# Revit family: RN 55044 Optipress-Therm-Vis de rappel
name_source: partatom
category: Rohrformteile
units: mm (PartAtom-declared; Revit-internal decimal feet)

## family parameters
Arbeitsebenenbasiert = Nein
Beim Laden mit Abzugskörper schneiden = Nein
Bemaßung runder Anschluss = Durchmesser verwenden
Gemeinsam genutzt = Nein
Immer vertikal = Ja
Teiletyp = Verbindung

## types (8) — shared parameters
1.010.00.2 Blattnummer der Richtlinie = 29
1.010.00.3 Ausgabedatum (Monat) der Richtlinie = 201308
1.010.00.4 Herstellername = R. Nussbaum AG
1.010.00.5 Revisionsdatum der Datei = 20190521
1.010.00.6 Webadresse des Herstellers = http://www.nussbaum.ch
1.100.00.4 Produktbezeichnung = Versorgung
1.110.00.2 Index = 1
1.110.00.4 Produktbezeichnung = Optipress-Therm
1.960/3L.00.8 Link (URL) = https://www.nussbaum.ch
29.700.00.4 Produktname = Optipress-Therm-Verschraubung, mit Innengewinde
29.700.00.5 Produktkennung = 2
29.700.00.6 Querschnittsform = 1
29.700.00.7 Nennweitensystem = DN
29.700.00.8 Nenndrucksystem = PN
29.710.02.4 Nenndruck = 16
29.710.02.5 max. zul. Überdruck [hPa] = 1600
29.710.02.7 max. zul. Dauer-Betriebsdruck [hPa] = 1600
29.710.02.9 max. zul. Dauer-Betriebstemperatur [°C] = 95
Connector Visibility = Nein
EnclosingSpace Visibility = Nein
Hersteller = R. Nussbaum AG

## per-type parameters (varying)
- DN=20x25: 1.800.00.3 TGA-Nummer=01900100000000000000000000000000000000000000000025000000000000000008; 1.800.00.4 Kommentarfeld=55044.30, Optipress-Therm-Verschraubung, mit Innengewinde, DN=20x25, L=77, Rp=1; 1.810.00.3 Hersteller-Bestellnummer=55044.3; 1.810.00.4 DATANORM-Nummer=55044.30; 1.810.00.5 StLB-Nummer=256.124; 1.810.00.6 GTIN-Nummer=7612945685797; 29.710.02.10 Formstück-Gewicht [kg]=0.252; 29.710.02.3 Benennung=Optipress-Therm-Verschraubung, mit Innengewinde, DN=20x25, L=77, Rp=1; CONNECTOR0_DIAMETER_dX_0r=20 mm; CONNECTOR0_dX_01=24 mm; CONNECTOR0_ref_dX=24 mm; CONNECTOR1_DIAMETER_dX_0r=25 mm  [stored 0.082021 ft]; CONNECTOR1_dX_00=60 mm; CONNECTOR1_dX_01=77 mm  [stored 0.252625 ft]; CONNECTOR1_ref_dX=60 mm; Modell=55044.3; R. Nussbaum AG 55044.22 de Visibility=Nein; R. Nussbaum AG 55044.23 de Visibility=Nein; R. Nussbaum AG 55044.25 de Visibility=Nein; R. Nussbaum AG 55044.26 de Visibility=Nein; R. Nussbaum AG 55044.27 de Visibility=Nein; R. Nussbaum AG 55044.28 de Visibility=Nein; R. Nussbaum AG 55044.29 de Visibility=Nein; R. Nussbaum AG 55044.30 de Visibility=Ja; Typenkommentare=Optipress-Therm-Vis de rappel DN=20x25
- DN=50: 1.800.00.3 TGA-Nummer=01900100000000000000000000000000000000000000000025000000000000000007; 1.800.00.4 Kommentarfeld=55044.29, Optipress-Therm-Verschraubung, mit Innengewinde, DN=50, L=87, Rp=2; 1.810.00.3 Hersteller-Bestellnummer=55044.29; 1.810.00.4 DATANORM-Nummer=55044.29; 1.810.00.5 StLB-Nummer=256.128; 1.810.00.6 GTIN-Nummer=7612945685834; 29.710.02.10 Formstück-Gewicht [kg]=0.801; 29.710.02.3 Benennung=Optipress-Therm-Verschraubung, mit Innengewinde, DN=50, L=87, Rp=2; CONNECTOR0_DIAMETER_dX_0r=50 mm; CONNECTOR0_dX_01=40 mm; CONNECTOR0_ref_dX=40 mm; CONNECTOR1_DIAMETER_dX_0r=50 mm; CONNECTOR1_dX_00=63 mm; CONNECTOR1_dX_01=87 mm; CONNECTOR1_ref_dX=63 mm; Modell=55044.29; R. Nussbaum AG 55044.22 de Visibility=Nein; R. Nussbaum AG 55044.23 de Visibility=Nein; R. Nussbaum AG 55044.25 de Visibility=Nein; R. Nussbaum AG 55044.26 de Visibility=Nein; R. Nussbaum AG 55044.27 de Visibility=Nein; R. Nussbaum AG 55044.28 de Visibility=Nein; R. Nussbaum AG 55044.29 de Visibility=Ja; R. Nussbaum AG 55044.30 de Visibility=Nein; Typenkommentare=Optipress-Therm-Vis de rappel DN=50
- DN=40: 1.800.00.3 TGA-Nummer=01900100000000000000000000000000000000000000000025000000000000000006; 1.800.00.4 Kommentarfeld=55044.28, Optipress-Therm-Verschraubung, mit Innengewinde, DN=40, L=91, Rp=1½; 1.810.00.3 Hersteller-Bestellnummer=55044.28; 1.810.00.4 DATANORM-Nummer=55044.28; 1.810.00.5 StLB-Nummer=256.127; 1.810.00.6 GTIN-Nummer=7612945685827; 29.710.02.10 Formstück-Gewicht [kg]=0.511; 29.710.02.3 Benennung=Optipress-Therm-Verschraubung, mit Innengewinde, DN=40, L=91, Rp=1½; CONNECTOR0_DIAMETER_dX_0r=40 mm; CONNECTOR0_dX_01=36 mm; CONNECTOR0_ref_dX=36 mm; CONNECTOR1_DIAMETER_dX_0r=40 mm; CONNECTOR1_dX_00=72 mm; CONNECTOR1_dX_01=91 mm; CONNECTOR1_ref_dX=72 mm; Modell=55044.28; R. Nussbaum AG 55044.22 de Visibility=Nein; R. Nussbaum AG 55044.23 de Visibility=Nein; R. Nussbaum AG 55044.25 de Visibility=Nein; R. Nussbaum AG 55044.26 de Visibility=Nein; R. Nussbaum AG 55044.27 de Visibility=Nein; R. Nussbaum AG 55044.28 de Visibility=Ja; R. Nussbaum AG 55044.29 de Visibility=Nein; R. Nussbaum AG 55044.30 de Visibility=Nein; Typenkommentare=Optipress-Therm-Vis de rappel DN=40
- DN=32: 1.800.00.3 TGA-Nummer=01900100000000000000000000000000000000000000000025000000000000000005; 1.800.00.4 Kommentarfeld=55044.27, Optipress-Therm-Verschraubung, mit Innengewinde, DN=32, L=78, Rp=1¼; 1.810.00.3 Hersteller-Bestellnummer=55044.27; 1.810.00.4 DATANORM-Nummer=55044.27; 1.810.00.5 StLB-Nummer=256.126; 1.810.00.6 GTIN-Nummer=7612945685810; 29.710.02.10 Formstück-Gewicht [kg]=0.359; 29.710.02.3 Benennung=Optipress-Therm-Verschraubung, mit Innengewinde, DN=32, L=78, Rp=1¼; CONNECTOR0_DIAMETER_dX_0r=32 mm; CONNECTOR0_dX_01=26 mm; CONNECTOR0_ref_dX=26 mm; CONNECTOR1_DIAMETER_dX_0r=32 mm; CONNECTOR1_dX_00=59 mm; CONNECTOR1_dX_01=78 mm; CONNECTOR1_ref_dX=59 mm; Modell=55044.27; R. Nussbaum AG 55044.22 de Visibility=Nein; R. Nussbaum AG 55044.23 de Visibility=Nein; R. Nussbaum AG 55044.25 de Visibility=Nein; R. Nussbaum AG 55044.26 de Visibility=Nein; R. Nussbaum AG 55044.27 de Visibility=Ja; R. Nussbaum AG 55044.28 de Visibility=Nein; R. Nussbaum AG 55044.29 de Visibility=Nein; R. Nussbaum AG 55044.30 de Visibility=Nein; Typenkommentare=Optipress-Therm-Vis de rappel DN=32
- DN=25: 1.800.00.3 TGA-Nummer=01900100000000000000000000000000000000000000000025000000000000000004; 1.800.00.4 Kommentarfeld=55044.26, Optipress-Therm-Verschraubung, mit Innengewinde, DN=25, L=88, Rp=1; 1.810.00.3 Hersteller-Bestellnummer=55044.26; 1.810.00.4 DATANORM-Nummer=55044.26; 1.810.00.5 StLB-Nummer=256.125; 1.810.00.6 GTIN-Nummer=7612945685803; 29.710.02.10 Formstück-Gewicht [kg]=0.278; 29.710.02.3 Benennung=Optipress-Therm-Verschraubung, mit Innengewinde, DN=25, L=88, Rp=1; CONNECTOR0_DIAMETER_dX_0r=25 mm  [stored 0.082021 ft]; CONNECTOR0_dX_01=24 mm; CONNECTOR0_ref_dX=24 mm; CONNECTOR1_DIAMETER_dX_0r=25 mm  [stored 0.082021 ft]; CONNECTOR1_dX_00=71 mm; CONNECTOR1_dX_01=88 mm; CONNECTOR1_ref_dX=71 mm; Modell=55044.26; R. Nussbaum AG 55044.22 de Visibility=Nein; R. Nussbaum AG 55044.23 de Visibility=Nein; R. Nussbaum AG 55044.25 de Visibility=Nein; R. Nussbaum AG 55044.26 de Visibility=Ja; R. Nussbaum AG 55044.27 de Visibility=Nein; R. Nussbaum AG 55044.28 de Visibility=Nein; R. Nussbaum AG 55044.29 de Visibility=Nein; R. Nussbaum AG 55044.30 de Visibility=Nein; Typenkommentare=Optipress-Therm-Vis de rappel DN=25
- DN=20: 1.800.00.3 TGA-Nummer=01900100000000000000000000000000000000000000000025000000000000000003; 1.800.00.4 Kommentarfeld=55044.25, Optipress-Therm-Verschraubung, mit Innengewinde, DN=20, L=76, Rp=¾; 1.810.00.3 Hersteller-Bestellnummer=55044.25; 1.810.00.4 DATANORM-Nummer=55044.25; 1.810.00.6 GTIN-Nummer=7612945685780; 29.710.02.10 Formstück-Gewicht [kg]=0.158; 29.710.02.3 Benennung=Optipress-Therm-Verschraubung, mit Innengewinde, DN=20, L=76, Rp=¾; CONNECTOR0_DIAMETER_dX_0r=20 mm; CONNECTOR0_dX_01=24 mm; CONNECTOR0_ref_dX=24 mm; CONNECTOR1_DIAMETER_dX_0r=20 mm; CONNECTOR1_dX_00=61 mm; CONNECTOR1_dX_01=76 mm; CONNECTOR1_ref_dX=61 mm; Modell=55044.25; R. Nussbaum AG 55044.22 de Visibility=Nein; R. Nussbaum AG 55044.23 de Visibility=Nein; R. Nussbaum AG 55044.25 de Visibility=Ja; R. Nussbaum AG 55044.26 de Visibility=Nein; R. Nussbaum AG 55044.27 de Visibility=Nein; R. Nussbaum AG 55044.28 de Visibility=Nein; R. Nussbaum AG 55044.29 de Visibility=Nein; R. Nussbaum AG 55044.30 de Visibility=Nein; Typenkommentare=Optipress-Therm-Vis de rappel DN=20
- DN=15: 1.800.00.3 TGA-Nummer=01900100000000000000000000000000000000000000000025000000000000000002; 1.800.00.4 Kommentarfeld=55044.23, Optipress-Therm-Verschraubung, mit Innengewinde, DN=15, L=65, Rp=½; 1.810.00.3 Hersteller-Bestellnummer=55044.23; 1.810.00.4 DATANORM-Nummer=55044.23; 1.810.00.6 GTIN-Nummer=7612945685773; 29.710.02.10 Formstück-Gewicht [kg]=0.125; 29.710.02.3 Benennung=Optipress-Therm-Verschraubung, mit Innengewinde, DN=15, L=65, Rp=½; CONNECTOR0_DIAMETER_dX_0r=15 mm  [stored 0.0492126 ft]; CONNECTOR0_dX_01=22 mm; CONNECTOR0_ref_dX=22 mm; CONNECTOR1_DIAMETER_dX_0r=15 mm  [stored 0.0492126 ft]; CONNECTOR1_dX_00=52 mm; CONNECTOR1_dX_01=65 mm; CONNECTOR1_ref_dX=52 mm; Modell=55044.23; R. Nussbaum AG 55044.22 de Visibility=Nein; R. Nussbaum AG 55044.23 de Visibility=Ja; R. Nussbaum AG 55044.25 de Visibility=Nein; R. Nussbaum AG 55044.26 de Visibility=Nein; R. Nussbaum AG 55044.27 de Visibility=Nein; R. Nussbaum AG 55044.28 de Visibility=Nein; R. Nussbaum AG 55044.29 de Visibility=Nein; R. Nussbaum AG 55044.30 de Visibility=Nein; Typenkommentare=Optipress-Therm-Vis de rappel DN=15
- DN=12x15: 1.800.00.3 TGA-Nummer=01900100000000000000000000000000000000000000000025000000000000000001; 1.800.00.4 Kommentarfeld=55044.22, Optipress-Therm-Verschraubung, mit Innengewinde, DN=12x15, L=64, Rp=½; 1.810.00.3 Hersteller-Bestellnummer=55044.22; 1.810.00.4 DATANORM-Nummer=55044.22; 1.810.00.5 StLB-Nummer=256.122; 1.810.00.6 GTIN-Nummer=7612945685766; 29.710.02.10 Formstück-Gewicht [kg]=0.123; 29.710.02.3 Benennung=Optipress-Therm-Verschraubung, mit Innengewinde, DN=12x15, L=64, Rp=½; CONNECTOR0_DIAMETER_dX_0r=12 mm  [stored 0.0393701 ft]; CONNECTOR0_dX_01=22 mm; CONNECTOR0_ref_dX=22 mm; CONNECTOR1_DIAMETER_dX_0r=15 mm  [stored 0.0492126 ft]; CONNECTOR1_dX_00=51 mm; CONNECTOR1_dX_01=64 mm; CONNECTOR1_ref_dX=51 mm; Modell=55044.22; R. Nussbaum AG 55044.22 de Visibility=Ja; R. Nussbaum AG 55044.23 de Visibility=Nein; R. Nussbaum AG 55044.25 de Visibility=Nein; R. Nussbaum AG 55044.26 de Visibility=Nein; R. Nussbaum AG 55044.27 de Visibility=Nein; R. Nussbaum AG 55044.28 de Visibility=Nein; R. Nussbaum AG 55044.29 de Visibility=Nein; R. Nussbaum AG 55044.30 de Visibility=Nein; Typenkommentare=Optipress-Therm-Vis de rappel DN=12x15

note: [stored X ft] marks values corroborated as IEEE doubles in the binary element streams (Revit-internal decimal feet)

## geometry (parser evidence)
native form markers: Sweep x1
no freeform markers — native parametric forms only
